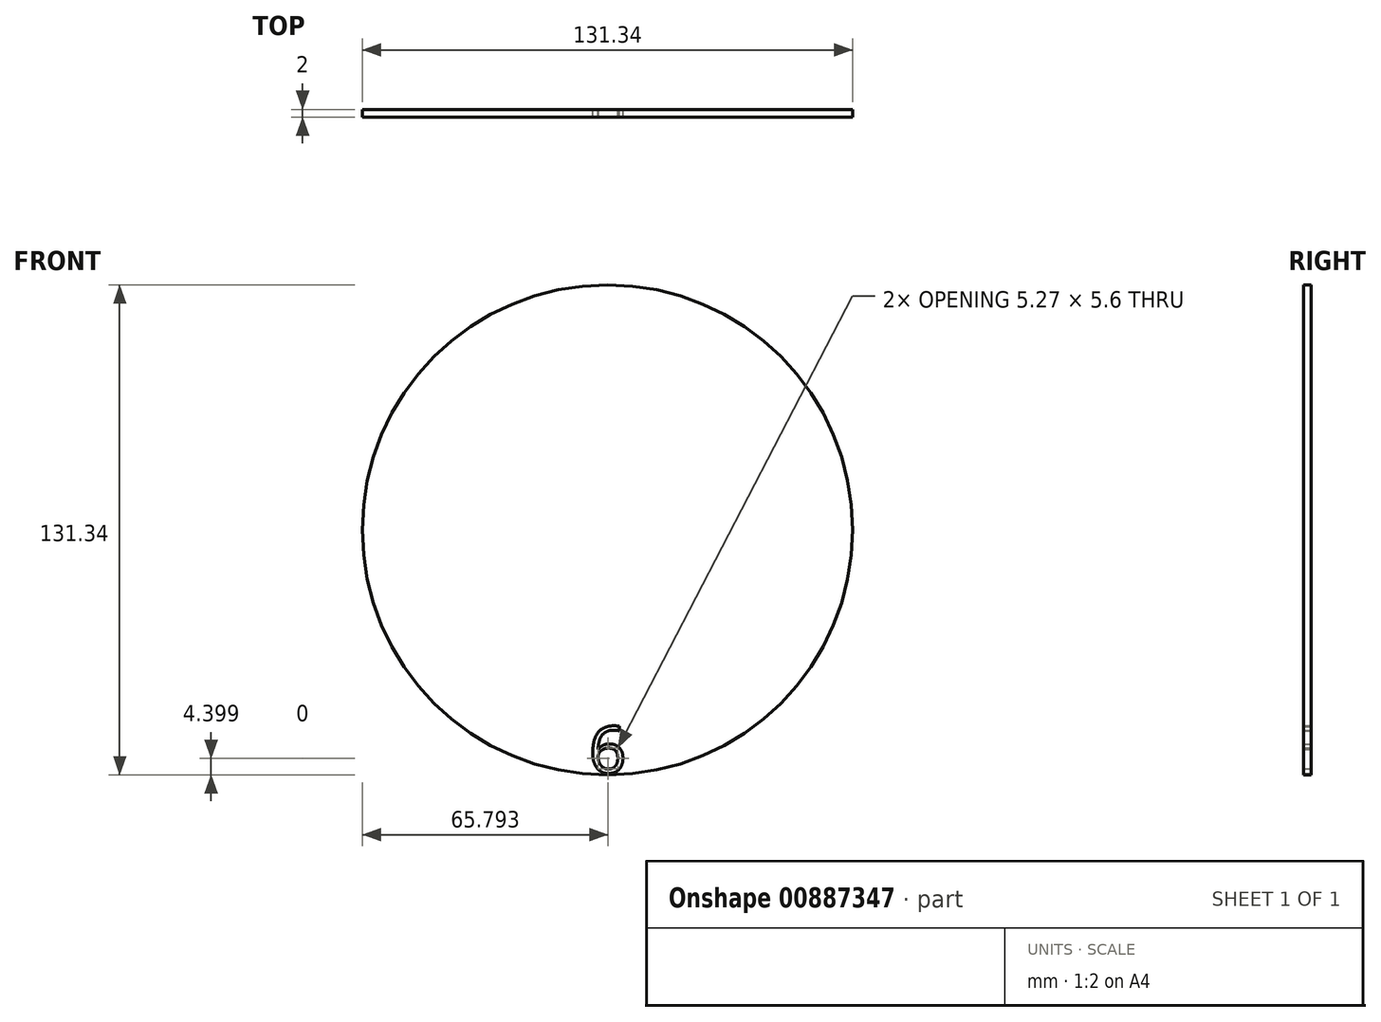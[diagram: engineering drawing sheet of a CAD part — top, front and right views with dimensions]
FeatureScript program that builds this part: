
annotation { "Feature Type Name" : "Feature", "Feature Type Description" : "" }
export const myFeature = defineFeature(function(context is Context, id is Id, definition is map)
    precondition{}
    {
        {
            var Q0;
            Q0=qCreatedBy(makeId("Front.planeOp"),FACE);
            var sketch = newSketch(context, id + "F0", { "sketchPlane" : qUnion([Q0])});
            skCircle(sketch, "E0", {"center": v(0, 0) * mm, "radius": 65.67 * mm});
            skSolve(sketch);
        }
        {
            var Q0;
            Q0=qCreatedBy(makeId("Front.planeOp"),FACE);
            var sketch = newSketch(context, id + "F1", { "sketchPlane" : qUnion([Q0])});
            skText(sketch, "E1", { "text": "6", "fontName": "OpenSans-Regular.ttf"});
            const initialGuessF1  = {"E1": [-0.00495, -0.0651, 1, 0, 0.01253]};
            skSetInitialGuess(sketch, initialGuessF1);
            skSolve(sketch);
        }
        {
            var Q0;
            Q0 = qSketchRegion(id + "F1", true);
            var Q1;
            Q1 = qSketchRegion(id + "F0", true);
            extrude(context, id + "F2", {"entities" : qUnion([Q0, Q1]), "depth" : 2 * mm, "offsetDistance" : 25 * mm});
        }
    });
